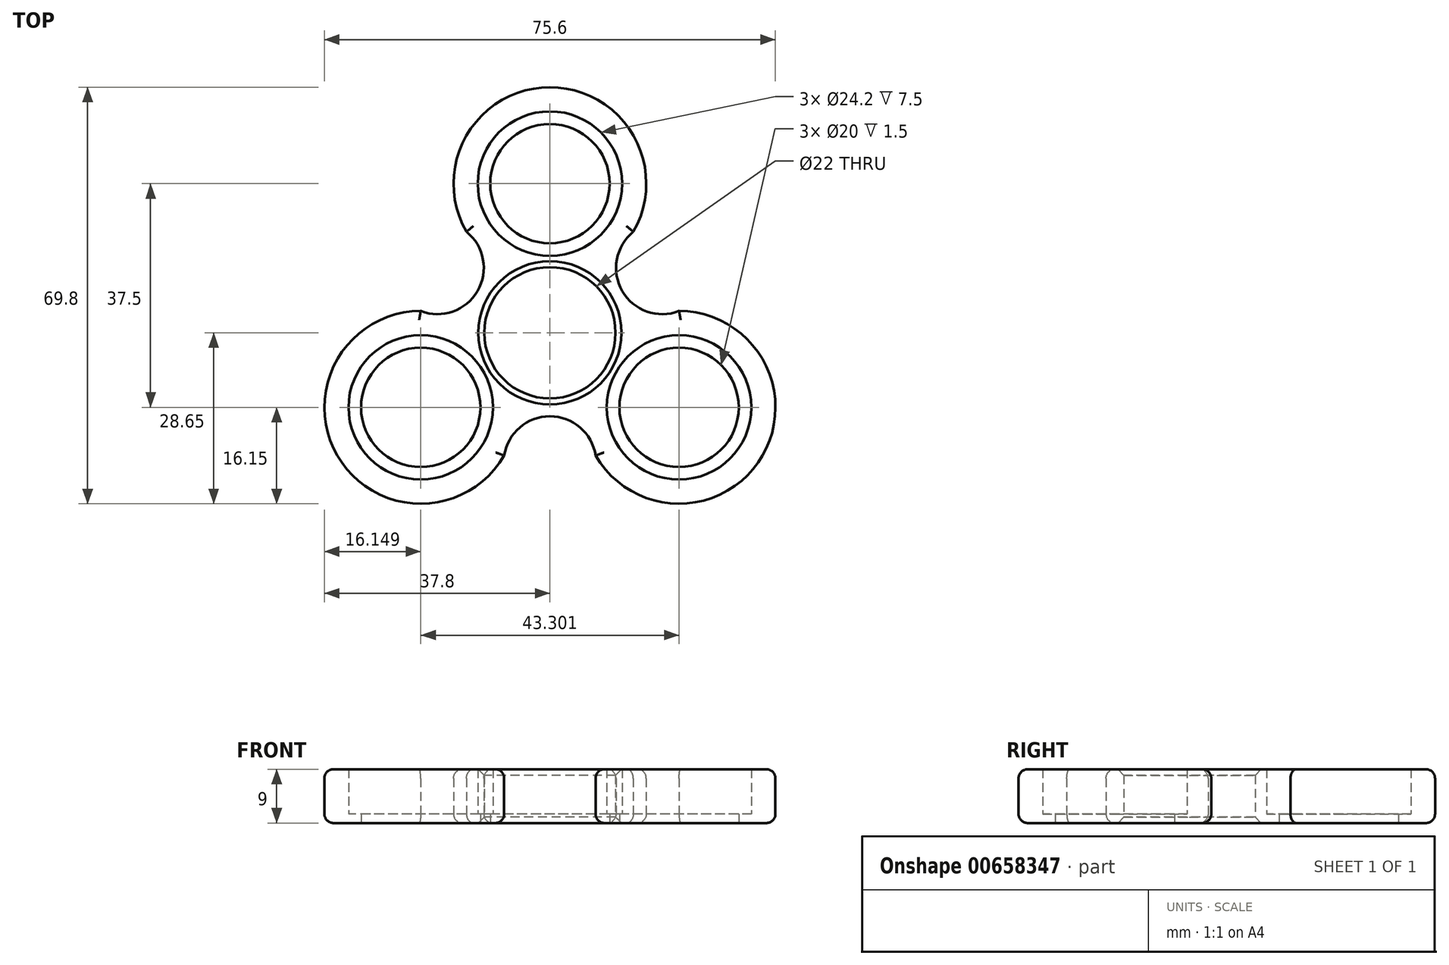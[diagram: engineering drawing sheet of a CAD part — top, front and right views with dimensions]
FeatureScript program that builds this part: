
annotation { "Feature Type Name" : "Feature", "Feature Type Description" : "" }
export const myFeature = defineFeature(function(context is Context, id is Id, definition is map)
    precondition{}
    {
        {
            var Q0;
            Q0=qCreatedBy(makeId("Top.planeOp"),FACE);
            var sketch = newSketch(context, id + "F0", { "sketchPlane" : qUnion([Q0])});
            skCircle(sketch, "E0", {"center": v(0, 27) * mm, "radius": 12.1 * mm});
            skPoint(sketch, "E1.center", {"position": v(0, 2) * mm});
            skCircle(sketch, "E2", {"center": v(0, 27) * mm, "radius": 10 * mm});
            skCircle(sketch, "E3", {"center": v(0, 2) * mm, "radius": 11 * mm});
            skArc(sketch, "E4.0", {"start": v(13.99, 18.92) * mm, "mid": v(0, 43.15) * mm, "end": v(-13.99, 18.93) * mm});
            skLineSegment(sketch, "E5", {"start": v(0, 27) * mm, "end": v(13.99, 18.92) * mm, "construction": true});
            skCircle(sketch, "E6.1.0", {"center": v(-21.65, -10.5) * mm, "radius": 10 * mm});
            skCircle(sketch, "E6.1.1", {"center": v(-21.65, -10.5) * mm, "radius": 12.1 * mm});
            skArc(sketch, "E6.1.2", {"start": v(-21.65, 5.65) * mm, "mid": v(-35.64, -18.57) * mm, "end": v(-7.66, -18.57) * mm});
            skLineSegment(sketch, "E6.1.3", {"start": v(-21.65, -10.5) * mm, "end": v(-21.65, 5.65) * mm, "construction": true});
            skLineSegment(sketch, "E6.1.4", {"start": v(-21.65, -10.5) * mm, "end": v(-7.66, -18.58) * mm, "construction": true});
            skCircle(sketch, "E6.2.0", {"center": v(21.65, -10.5) * mm, "radius": 10 * mm});
            skCircle(sketch, "E6.2.1", {"center": v(21.65, -10.5) * mm, "radius": 12.1 * mm});
            skArc(sketch, "E6.2.2", {"start": v(7.66, -18.58) * mm, "mid": v(35.64, -18.58) * mm, "end": v(21.65, 5.65) * mm});
            skLineSegment(sketch, "E6.2.3", {"start": v(21.65, -10.5) * mm, "end": v(7.66, -18.58) * mm, "construction": true});
            skLineSegment(sketch, "E6.2.4", {"start": v(21.65, -10.5) * mm, "end": v(21.65, 5.65) * mm, "construction": true});
            skPoint(sketch, "E7.orphan", {"position": v(-11.33, 15.5) * mm});
            skPoint(sketch, "E8.orphan", {"position": v(11.5, 15.67) * mm});
            skPoint(sketch, "E9.orphan", {"position": v(-17.6, 5.13) * mm});
            skPoint(sketch, "E10.orphan", {"position": v(-6.02, -14.56) * mm});
            skPoint(sketch, "E11.orphan", {"position": v(17.35, 5.07) * mm});
            skPoint(sketch, "E12.orphan", {"position": v(6.08, -14.8) * mm});
            skLineSegment(sketch, "E13", {"start": v(9.53, 7.5) * mm, "end": v(12.12, 9) * mm});
            skArc(sketch, "E14", {"start": v(13.99, 18.92) * mm, "mid": v(12.12, 9) * mm, "end": v(21.65, 5.65) * mm});
            skArc(sketch, "E15.1.0", {"start": v(-21.65, 5.65) * mm, "mid": v(-12.12, 9) * mm, "end": v(-13.99, 18.93) * mm});
            skArc(sketch, "E15.2.0", {"start": v(7.66, -18.58) * mm, "mid": v(0, -12) * mm, "end": v(-7.66, -18.57) * mm});
            skSolve(sketch);
        }
        {
            var Q0;
            Q0=makeQuery(id+"F0.imprint","IMPRINT",FACE,{"disambiguationData":[TD([[makeQuery(id+"F0.imprint","IMPRINT",EDGE,{"derivedFrom":sQuery(id+"F0.wireOp",EDGE,"E0")}),-1.0]])]});
            extrude(context, id + "F1", {"entities" : qUnion([Q0]), "depth" : 9 * mm, "offsetDistance" : 25 * mm});
        }
        {
            var Q0;
            Q0=makeQuery(id+"F0.imprint","IMPRINT",FACE,{"disambiguationData":[TD([[makeQuery(id+"F0.imprint","IMPRINT",EDGE,{"derivedFrom":sQuery(id+"F0.wireOp",EDGE,"E0")}),1.0]])]});
            var Q1;
            Q1=makeQuery(id+"F0.imprint","IMPRINT",FACE,{"disambiguationData":[TD([[makeQuery(id+"F0.imprint","IMPRINT",EDGE,{"derivedFrom":sQuery(id+"F0.wireOp",EDGE,"E6.1.0")}),-1.0]])]});
            var Q2;
            Q2=makeQuery(id+"F0.imprint","IMPRINT",FACE,{"disambiguationData":[TD([[makeQuery(id+"F0.imprint","IMPRINT",EDGE,{"derivedFrom":sQuery(id+"F0.wireOp",EDGE,"E6.2.0")}),-1.0]])]});
            extrude(context, id + "F2", {"entities" : qUnion([Q0, Q1, Q2]), "operationType" : NewBodyOperationType.ADD, "depth" : 1.5 * mm, "offsetDistance" : 25 * mm});
        }
        {
            var Q0;
            Q0=makeQuery(id+"F1.opExtrude","CAP_EDGE",EDGE,{"disambiguationData":[OSD([sQuery(id+"F0.wireOp",EDGE,"E6.1.2")])],"isStart":false});
            var Q1;
            Q1=makeQuery(id+"F1.opExtrude","CAP_EDGE",EDGE,{"disambiguationData":[OSD([sQuery(id+"F0.wireOp",EDGE,"E15.2.0")])],"isStart":false});
            var Q2;
            Q2=makeQuery(id+"F1.opExtrude","CAP_EDGE",EDGE,{"disambiguationData":[OSD([sQuery(id+"F0.wireOp",EDGE,"E6.2.2")])],"isStart":false});
            var Q3;
            Q3=makeQuery(id+"F1.opExtrude","CAP_EDGE",EDGE,{"disambiguationData":[OSD([sQuery(id+"F0.wireOp",EDGE,"E14")])],"isStart":false});
            var Q4;
            Q4=makeQuery(id+"F1.opExtrude","CAP_EDGE",EDGE,{"disambiguationData":[OSD([sQuery(id+"F0.wireOp",EDGE,"E4.0")])],"isStart":false});
            var Q5;
            Q5=makeQuery(id+"F1.opExtrude","CAP_EDGE",EDGE,{"disambiguationData":[OSD([sQuery(id+"F0.wireOp",EDGE,"E15.1.0")])],"isStart":false});
            fillet(context, id + "F3", {"entities" : qUnion([Q0, Q1, Q2, Q3, Q4, Q5]), "radius" : 1.5 * mm, "tangentPropagation" : true, "allowEdgeOverflow" : false});
        }
        {
            var Q0;
            Q0=makeQuery(id+"F1.opExtrude","CAP_EDGE",EDGE,{"disambiguationData":[OSD([sQuery(id+"F0.wireOp",EDGE,"E6.1.2")])],"isStart":true});
            var Q1;
            Q1=makeQuery(id+"F1.opExtrude","CAP_EDGE",EDGE,{"disambiguationData":[OSD([sQuery(id+"F0.wireOp",EDGE,"E15.2.0")])],"isStart":true});
            var Q2;
            Q2=makeQuery(id+"F1.opExtrude","CAP_EDGE",EDGE,{"disambiguationData":[OSD([sQuery(id+"F0.wireOp",EDGE,"E6.2.2")])],"isStart":true});
            var Q3;
            Q3=makeQuery(id+"F1.opExtrude","CAP_EDGE",EDGE,{"disambiguationData":[OSD([sQuery(id+"F0.wireOp",EDGE,"E14")])],"isStart":true});
            var Q4;
            Q4=makeQuery(id+"F1.opExtrude","CAP_EDGE",EDGE,{"disambiguationData":[OSD([sQuery(id+"F0.wireOp",EDGE,"E4.0")])],"isStart":true});
            var Q5;
            Q5=makeQuery(id+"F1.opExtrude","CAP_EDGE",EDGE,{"disambiguationData":[OSD([sQuery(id+"F0.wireOp",EDGE,"E15.1.0")])],"isStart":true});
            fillet(context, id + "F4", {"entities" : qUnion([Q0, Q1, Q2, Q3, Q4, Q5]), "radius" : 1.5 * mm, "tangentPropagation" : true, "allowEdgeOverflow" : false});
        }
        {
            var Q0;
            Q0=makeQuery(id+"F1.opExtrude","CAP_EDGE",EDGE,{"disambiguationData":[OSD([sQuery(id+"F0.wireOp",EDGE,"E3")])],"isStart":false});
            var Q1;
            Q1=makeQuery(id+"F1.opExtrude","CAP_EDGE",EDGE,{"disambiguationData":[OSD([sQuery(id+"F0.wireOp",EDGE,"E3")])],"isStart":true});
            chamfer(context, id + "F5", {"entities" : qUnion([Q0, Q1]), "width" : 1 * mm, "tangentPropagation" : true});
        }
    });
